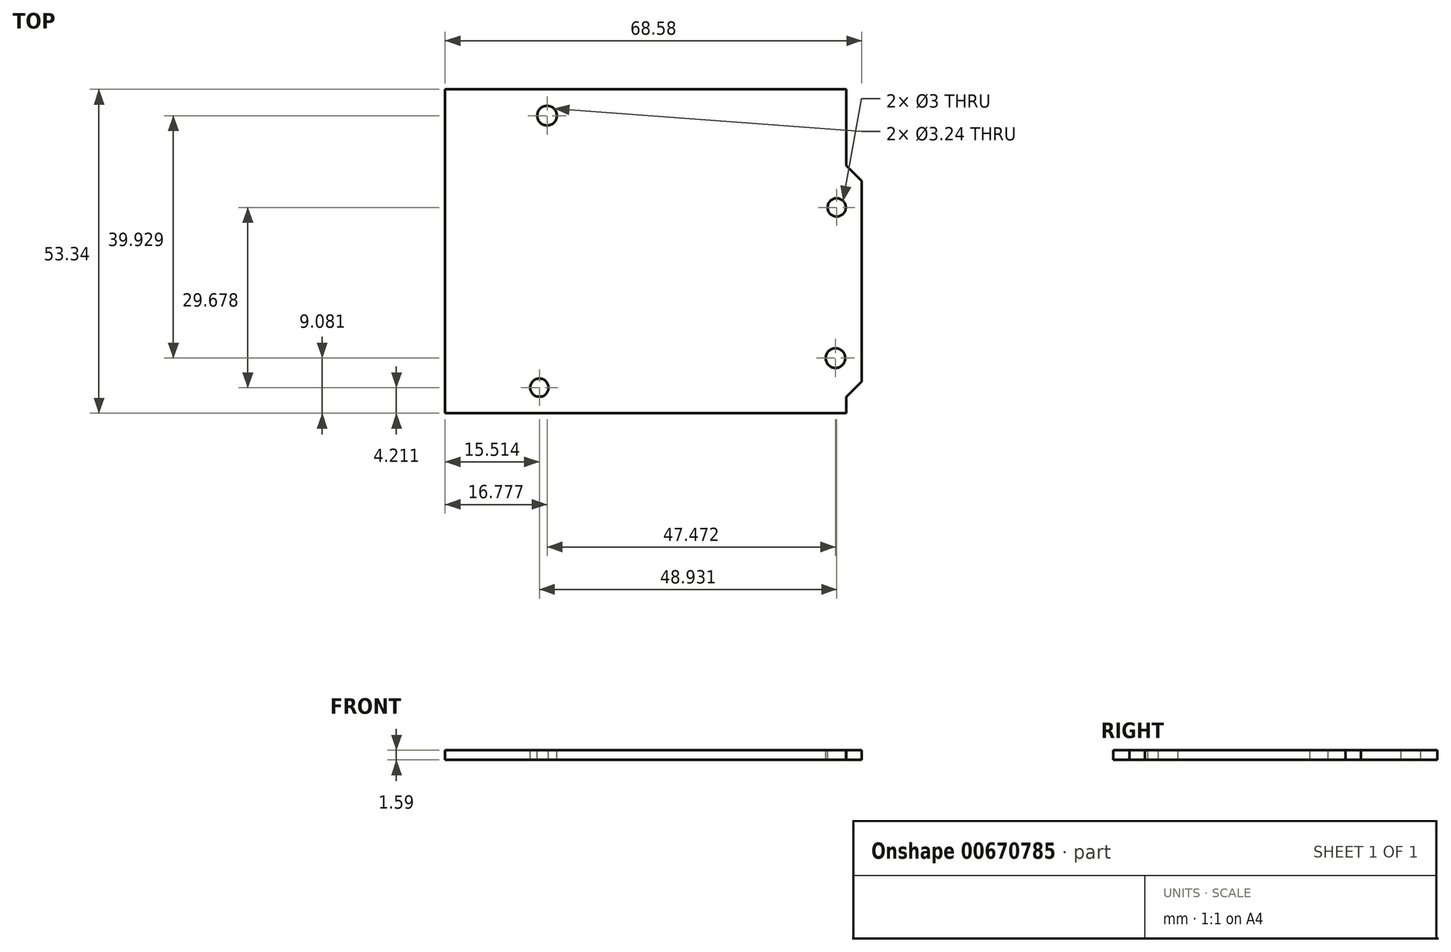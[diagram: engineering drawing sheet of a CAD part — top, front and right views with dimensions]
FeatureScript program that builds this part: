
annotation { "Feature Type Name" : "Feature", "Feature Type Description" : "" }
export const myFeature = defineFeature(function(context is Context, id is Id, definition is map)
    precondition{}
    {
        {
            var Q0;
            Q0=qCreatedBy(makeId("Top.planeOp"),FACE);
            var sketch = newSketch(context, id + "F0", { "sketchPlane" : qUnion([Q0])});
            skLineSegment(sketch, "E0", {"start": v(-33.02, 26.67) * mm, "end": v(33.02, 26.67) * mm});
            skLineSegment(sketch, "E1", {"start": v(-33.02, 26.67) * mm, "end": v(-33.02, -26.67) * mm});
            skLineSegment(sketch, "E2", {"start": v(-33.02, -26.67) * mm, "end": v(33.02, -26.67) * mm});
            skLineSegment(sketch, "E3", {"start": v(33.02, 26.67) * mm, "end": v(33.02, -26.67) * mm});
            skLineSegment(sketch, "E4", {"start": v(33.02, -24) * mm, "end": v(35.56, -21.46) * mm});
            skLineSegment(sketch, "E5", {"start": v(35.56, -21.46) * mm, "end": v(35.56, 11.56) * mm});
            skLineSegment(sketch, "E6", {"start": v(35.56, 11.56) * mm, "end": v(33.02, 14.1) * mm});
            skLineSegment(sketch, "E7", {"start": v(0, 0) * mm, "end": v(0, 26.67) * mm, "construction": true});
            skLineSegment(sketch, "E8", {"start": v(0, 0) * mm, "end": v(-33.02, 0) * mm, "construction": true});
            skSolve(sketch);
        }
        {
            var Q0;
            {var subQ0=sQuery(id+"F0.wireOp",EDGE,"E4");Q0=makeQuery(id+"F0.imprint","IMPRINT",FACE,{"disambiguationData":[TD([[makeQuery(id+"F0.imprint","IMPRINT",EDGE,{"derivedFrom":subQ0}),1.0]])]});}
            var Q1;
            {var subQ1=sQuery(id+"F0.wireOp",EDGE,"E0");Q1=makeQuery(id+"F0.imprint","IMPRINT",FACE,{"disambiguationData":[TD([[makeQuery(id+"F0.imprint","IMPRINT",EDGE,{"derivedFrom":subQ1}),-1.0]])]});}
            extrude(context, id + "F1", {"entities" : qUnion([Q0, Q1]), "depth" : 1.59 * mm, "offsetDistance" : 25 * mm});
        }
        {
            var Q0;
            Q0=makeQuery(id+"F1.opExtrude","CAP_FACE",FACE,{"disambiguationData":[OSD([sQuery(id+"F0.wireOp",EDGE,"E0"),sQuery(id+"F0.wireOp",EDGE,"E1"),sQuery(id+"F0.wireOp",EDGE,"E2"),sQuery(id+"F0.wireOp",EDGE,"E3"),sQuery(id+"F0.wireOp",EDGE,"E4"),sQuery(id+"F0.wireOp",EDGE,"E5"),sQuery(id+"F0.wireOp",EDGE,"E6")])],"isStart":false});
            var sketch = newSketch(context, id + "F2", { "sketchPlane" : qUnion([Q0])});
            skCircle(sketch, "E9", {"center": v(-16.24, 22.34) * mm, "radius": 1.62 * mm});
            skCircle(sketch, "E10", {"center": v(-17.5, -22.46) * mm, "radius": 1.5 * mm});
            skCircle(sketch, "E11", {"center": v(31.23, -17.59) * mm, "radius": 1.62 * mm});
            skCircle(sketch, "E12", {"center": v(31.42, 7.22) * mm, "radius": 1.5 * mm});
            skSolve(sketch);
        }
        {
            var Q0;
            Q0 = qSketchRegion(id + "F2", true);
            extrude(context, id + "F3", {"entities" : qUnion([Q0]), "operationType" : NewBodyOperationType.REMOVE, "oppositeDirection" : true, "depth" : 1.59 * mm, "offsetDistance" : 25 * mm});
        }
    });
